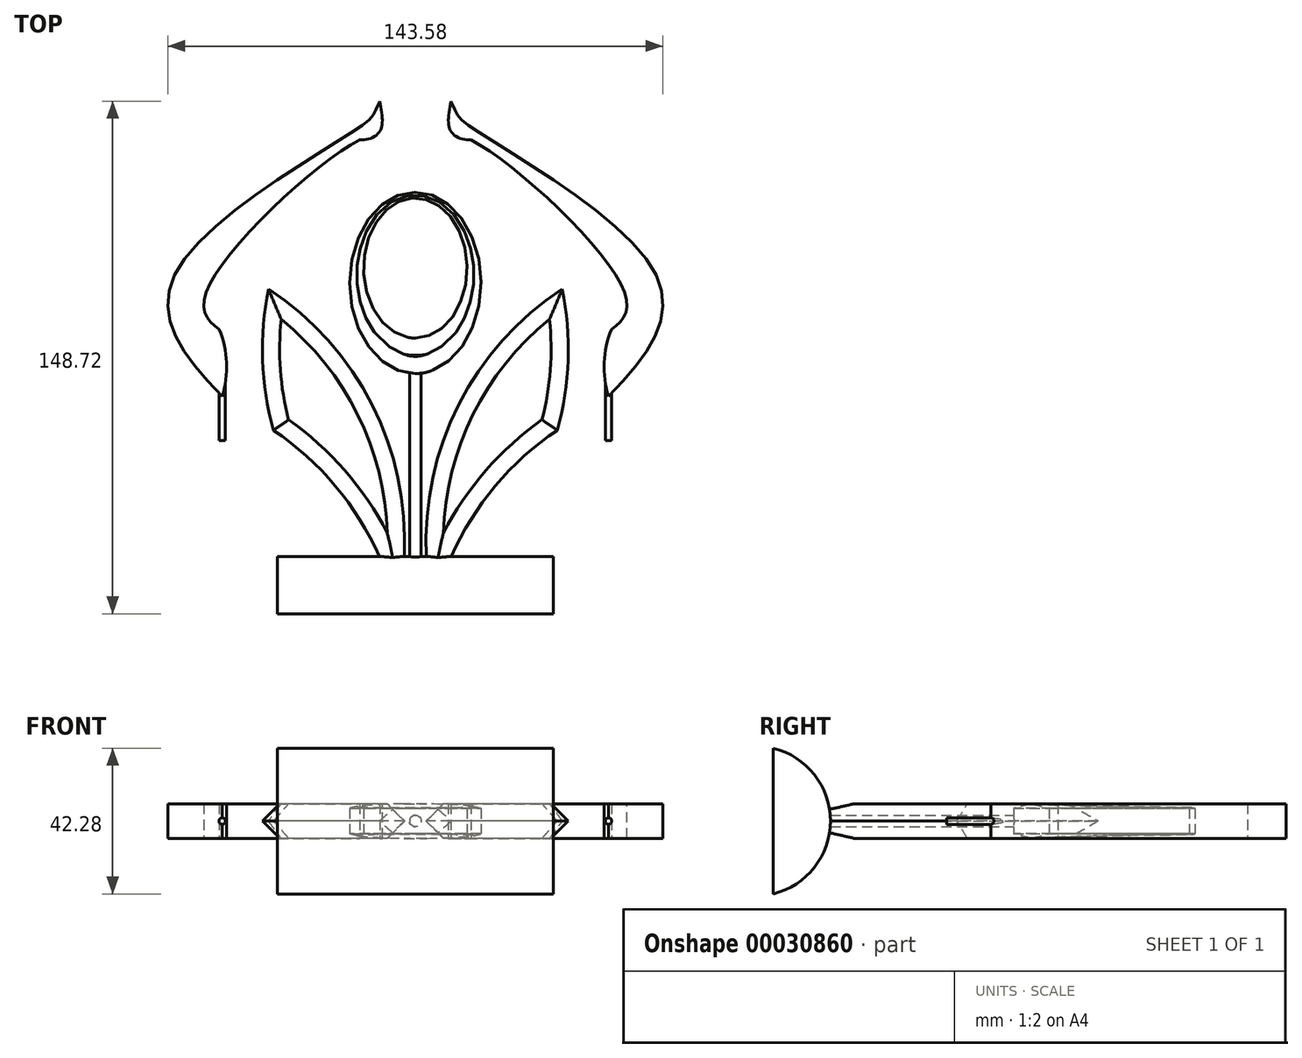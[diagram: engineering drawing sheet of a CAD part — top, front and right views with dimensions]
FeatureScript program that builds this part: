
annotation { "Feature Type Name" : "Feature", "Feature Type Description" : "" }
export const myFeature = defineFeature(function(context is Context, id is Id, definition is map)
    precondition{}
    {
        {
            var Q0;
            Q0=qCreatedBy(makeId("Top.planeOp"),FACE);
            var sketch = newSketch(context, id + "F0", { "sketchPlane" : qUnion([Q0])});
            skLineSegment(sketch, "E0", {"start": v(-75.5, -12.71) * mm, "end": v(-9.56, -74.3) * mm, "construction": true});
            skLineSegment(sketch, "E1", {"start": v(-4.86, -71.61) * mm, "end": v(-42.6, 18.94) * mm, "construction": true});
            skArc(sketch, "E2", {"start": v(-75.5, -12.71) * mm, "mid": v(-51.74, -53.37) * mm, "end": v(-9.56, -74.3) * mm});
            skArc(sketch, "E3", {"start": v(-4.86, -71.61) * mm, "mid": v(-9.83, -20.55) * mm, "end": v(-42.6, 18.94) * mm});
            skArc(sketch, "E4.MirrorCS", {"start": v(-75.5, -12.71) * mm, "mid": v(-33.32, -33.65) * mm, "end": v(-9.56, -74.3) * mm});
            skArc(sketch, "E5.0", {"start": v(-41.12, -22.06) * mm, "mid": v(-19.25, -43.28) * mm, "end": v(-6.12, -70.78) * mm});
            skArc(sketch, "E6.MirrorCS", {"start": v(-4.86, -71.61) * mm, "mid": v(-5.5, -71.2) * mm, "end": v(-6.12, -70.78) * mm});
            skArc(sketch, "E7.trimOffspring", {"start": v(-41.12, -22.06) * mm, "mid": v(-44.3, -1.65) * mm, "end": v(-42.6, 18.94) * mm});
            skArc(sketch, "E8.MirrorCS", {"start": v(75.5, -12.71) * mm, "mid": v(51.74, -53.37) * mm, "end": v(9.56, -74.3) * mm});
            skArc(sketch, "E9.MirrorCS", {"start": v(75.5, -12.71) * mm, "mid": v(33.32, -33.65) * mm, "end": v(9.56, -74.3) * mm});
            skArc(sketch, "E10.MirrorCS", {"start": v(41.12, -22.06) * mm, "mid": v(44.3, -1.65) * mm, "end": v(42.6, 18.94) * mm});
            skArc(sketch, "E11.MirrorCS", {"start": v(41.12, -22.06) * mm, "mid": v(19.25, -43.28) * mm, "end": v(6.12, -70.78) * mm});
            skArc(sketch, "E12.MirrorCS", {"start": v(4.86, -71.61) * mm, "mid": v(9.83, -20.55) * mm, "end": v(42.6, 18.94) * mm});
            skArc(sketch, "E13.MirrorCS", {"start": v(4.86, -71.61) * mm, "mid": v(5.5, -71.2) * mm, "end": v(6.12, -70.78) * mm});
            skSolve(sketch);
        }
        {
            var Q0;
            Q0=qCreatedBy(makeId("Top.planeOp"),FACE);
            var sketch = newSketch(context, id + "F1", { "sketchPlane" : qUnion([Q0])});
            skEllipse(sketch, "E14", {"center": v(0, 20.7) * mm, "majorRadius": 26.3 * mm, "minorRadius": 19.05 * mm, "majorAxis": v(0, -1)});
            skEllipse(sketch, "E15", {"center": v(0, 25) * mm, "majorRadius": 20.32 * mm, "minorRadius": 15 * mm, "majorAxis": v(0, -1)});
            skSolve(sketch);
        }
        {
            var Q0;
            Q0=qCreatedBy(makeId("Top.planeOp"),FACE);
            var sketch = newSketch(context, id + "F2", { "sketchPlane" : qUnion([Q0])});
            skFitSpline(sketch, "E16", {"points": [v(-10.32, 73.44) * mm, v(-14.62, 66.99) * mm, v(-69.19, 24.14) * mm, v(-56, -12.24) * mm], "startDerivative": vector(-33.58, -68.78) * mm, "endDerivative": vector(100.58, -102.34) * mm});
            skArc(sketch, "E17", {"start": v(-56, -12.24) * mm, "mid": v(-54.75, -2.43) * mm, "end": v(-56.87, 7.24) * mm});
            skFitSpline(sketch, "E18", {"points": [v(-56.87, 7.24) * mm, v(-60.9, 17.24) * mm, v(-16.13, 62.2) * mm], "startDerivative": vector(-32.39, 22.42) * mm, "endDerivative": vector(56.1, 28.88) * mm});
            skFitSpline(sketch, "E19", {"points": [v(-10.32, 73.44) * mm, v(-10.32, 64.63) * mm, v(-16.13, 62.2) * mm], "startDerivative": vector(3.32, -19.88) * mm, "endDerivative": vector(-13.95, 1.21) * mm});
            skFitSpline(sketch, "E20.MirrorCS", {"points": [v(10.32, 73.44) * mm, v(10.32, 64.63) * mm, v(16.13, 62.2) * mm], "startDerivative": vector(-3.32, -19.88) * mm, "endDerivative": vector(13.95, 1.21) * mm});
            skFitSpline(sketch, "E21.MirrorCS", {"points": [v(10.32, 73.44) * mm, v(14.62, 66.99) * mm, v(69.19, 24.14) * mm, v(56, -12.24) * mm], "startDerivative": vector(33.58, -68.78) * mm, "endDerivative": vector(-100.58, -102.34) * mm});
            skFitSpline(sketch, "E22.MirrorCS", {"points": [v(56.87, 7.24) * mm, v(60.9, 17.24) * mm, v(16.13, 62.2) * mm], "startDerivative": vector(32.39, 22.42) * mm, "endDerivative": vector(-56.1, 28.88) * mm});
            skArc(sketch, "E23.MirrorCS", {"start": v(56, -12.24) * mm, "mid": v(54.75, -2.43) * mm, "end": v(56.87, 7.24) * mm});
            skSolve(sketch);
        }
        {
            var Q0;
            Q0=makeQuery(id+"F2.imprint","IMPRINT",FACE,{"disambiguationData":[TD([[makeQuery(id+"F2.imprint","IMPRINT",EDGE,{"derivedFrom":sQuery(id+"F2.wireOp",EDGE,"E16")}),1.0]])]});
            var Q1;
            Q1=makeQuery(id+"F2.imprint","IMPRINT",FACE,{"disambiguationData":[TD([[makeQuery(id+"F2.imprint","IMPRINT",EDGE,{"derivedFrom":sQuery(id+"F2.wireOp",EDGE,"E20.MirrorCS")}),1.0]])]});
            var Q2;
            Q2=makeQuery(id+"F0.imprint","IMPRINT",FACE,{"disambiguationData":[TD([[makeQuery(id+"F0.imprint","IMPRINT",EDGE,{"derivedFrom":sQuery(id+"F0.wireOp",EDGE,"E3")}),1.0]])]});
            var Q3;
            Q3=makeQuery(id+"F0.imprint","IMPRINT",FACE,{"disambiguationData":[TD([[makeQuery(id+"F0.imprint","IMPRINT",EDGE,{"derivedFrom":sQuery(id+"F0.wireOp",EDGE,"E4.MirrorCS")}),-1.0]])]});
            var Q4;
            Q4=makeQuery(id+"F0.imprint","IMPRINT",FACE,{"disambiguationData":[TD([[makeQuery(id+"F0.imprint","IMPRINT",EDGE,{"derivedFrom":sQuery(id+"F0.wireOp",EDGE,"E10.MirrorCS")}),1.0]])]});
            var Q5;
            Q5=makeQuery(id+"F0.imprint","IMPRINT",FACE,{"disambiguationData":[TD([[makeQuery(id+"F0.imprint","IMPRINT",EDGE,{"derivedFrom":sQuery(id+"F0.wireOp",EDGE,"E8.MirrorCS")}),-1.0]])]});
            var Q6;
            Q6=makeQuery(id+"F1.imprint","IMPRINT",FACE,{"disambiguationData":[TD([[makeQuery(id+"F1.imprint","IMPRINT",EDGE,{"derivedFrom":sQuery(id+"F1.wireOp",EDGE,"E14")}),1.0]])]});
            extrude(context, id + "F3", {"entities" : qUnion([Q0, Q1, Q2, Q3, Q4, Q5, Q6]), "endBound" : BoundingType.SYMMETRIC, "depth" : 10 * mm});
        }
        {
            var Q0;
            Q0=makeQuery(id+"F3.opExtrude","CAP_FACE",FACE,{"disambiguationData":[OSD([sQuery(id+"F0.wireOp",EDGE,"E4.MirrorCS"),sQuery(id+"F0.wireOp",EDGE,"E2")])],"isStart":false});
            var Q1;
            Q1=makeQuery(id+"F3.opExtrude","CAP_FACE",FACE,{"disambiguationData":[OSD([sQuery(id+"F0.wireOp",EDGE,"E3"),sQuery(id+"F0.wireOp",EDGE,"E5.0"),sQuery(id+"F0.wireOp",EDGE,"E6.MirrorCS"),sQuery(id+"F0.wireOp",EDGE,"E7.trimOffspring")])],"isStart":false});
            var Q2;
            Q2=makeQuery(id+"F3.opExtrude","CAP_FACE",FACE,{"disambiguationData":[OSD([sQuery(id+"F0.wireOp",EDGE,"E10.MirrorCS"),sQuery(id+"F0.wireOp",EDGE,"E11.MirrorCS"),sQuery(id+"F0.wireOp",EDGE,"E12.MirrorCS"),sQuery(id+"F0.wireOp",EDGE,"E13.MirrorCS")])],"isStart":false});
            var Q3;
            Q3=makeQuery(id+"F3.opExtrude","CAP_FACE",FACE,{"disambiguationData":[OSD([sQuery(id+"F0.wireOp",EDGE,"E8.MirrorCS"),sQuery(id+"F0.wireOp",EDGE,"E9.MirrorCS")])],"isStart":false});
            var Q4;
            Q4=makeQuery(id+"F3.opExtrude","CAP_FACE",FACE,{"disambiguationData":[OSD([sQuery(id+"F0.wireOp",EDGE,"E8.MirrorCS"),sQuery(id+"F0.wireOp",EDGE,"E9.MirrorCS")])],"isStart":true});
            var Q5;
            Q5=makeQuery(id+"F3.opExtrude","CAP_FACE",FACE,{"disambiguationData":[OSD([sQuery(id+"F0.wireOp",EDGE,"E10.MirrorCS"),sQuery(id+"F0.wireOp",EDGE,"E11.MirrorCS"),sQuery(id+"F0.wireOp",EDGE,"E12.MirrorCS"),sQuery(id+"F0.wireOp",EDGE,"E13.MirrorCS")])],"isStart":true});
            var Q6;
            Q6=makeQuery(id+"F3.opExtrude","CAP_FACE",FACE,{"disambiguationData":[OSD([sQuery(id+"F0.wireOp",EDGE,"E3"),sQuery(id+"F0.wireOp",EDGE,"E5.0"),sQuery(id+"F0.wireOp",EDGE,"E6.MirrorCS"),sQuery(id+"F0.wireOp",EDGE,"E7.trimOffspring")])],"isStart":true});
            var Q7;
            Q7=makeQuery(id+"F3.opExtrude","CAP_FACE",FACE,{"disambiguationData":[OSD([sQuery(id+"F0.wireOp",EDGE,"E4.MirrorCS"),sQuery(id+"F0.wireOp",EDGE,"E2")])],"isStart":true});
            chamfer(context, id + "F4", {"entities" : qUnion([Q0, Q1, Q2, Q3, Q4, Q5, Q6, Q7]), "width" : 5 * mm, "tangentPropagation" : true});
        }
        {
            var Q0;
            Q0=makeQuery(id+"F3.opExtrude","CAP_FACE",FACE,{"disambiguationData":[OSD([sQuery(id+"F2.wireOp",EDGE,"E16"),sQuery(id+"F2.wireOp",EDGE,"E17"),sQuery(id+"F2.wireOp",EDGE,"E18"),sQuery(id+"F2.wireOp",EDGE,"E19")])],"isStart":false});
            var Q1;
            Q1=makeQuery(id+"F3.opExtrude","CAP_FACE",FACE,{"disambiguationData":[OSD([sQuery(id+"F2.wireOp",EDGE,"E20.MirrorCS"),sQuery(id+"F2.wireOp",EDGE,"E21.MirrorCS"),sQuery(id+"F2.wireOp",EDGE,"E22.MirrorCS"),sQuery(id+"F2.wireOp",EDGE,"E23.MirrorCS")])],"isStart":false});
            var Q2;
            Q2=makeQuery(id+"F3.opExtrude","CAP_FACE",FACE,{"disambiguationData":[OSD([sQuery(id+"F2.wireOp",EDGE,"E16"),sQuery(id+"F2.wireOp",EDGE,"E17"),sQuery(id+"F2.wireOp",EDGE,"E18"),sQuery(id+"F2.wireOp",EDGE,"E19")])],"isStart":true});
            var Q3;
            Q3=makeQuery(id+"F3.opExtrude","CAP_FACE",FACE,{"disambiguationData":[OSD([sQuery(id+"F2.wireOp",EDGE,"E20.MirrorCS"),sQuery(id+"F2.wireOp",EDGE,"E21.MirrorCS"),sQuery(id+"F2.wireOp",EDGE,"E22.MirrorCS"),sQuery(id+"F2.wireOp",EDGE,"E23.MirrorCS")])],"isStart":true});
            var Q4;
            Q4=makeQuery(id+"F3.opExtrude","CAP_FACE",FACE,{"disambiguationData":[OSD([sQuery(id+"F1.wireOp",EDGE,"E14"),sQuery(id+"F1.wireOp",EDGE,"E15")])],"isStart":true});
            var Q5;
            Q5=makeQuery(id+"F3.opExtrude","CAP_FACE",FACE,{"disambiguationData":[OSD([sQuery(id+"F1.wireOp",EDGE,"E14"),sQuery(id+"F1.wireOp",EDGE,"E15")])],"isStart":false});
            chamfer(context, id + "F5", {"entities" : qUnion([Q0, Q1, Q2, Q3, Q4, Q5]), "chamferType" : ChamferType.TWO_OFFSETS, "width1" : 1.3 * mm, "oppositeDirection" : false, "width2" : 5 * mm, "tangentPropagation" : true});
        }
        {
            var Q0;
            Q0=qCreatedBy(makeId("Right.planeOp"),FACE);
            var sketch = newSketch(context, id + "F6", { "sketchPlane" : qUnion([Q0])});
            skArc(sketch, "E24", {"start": v(-75.28, -21.14) * mm, "mid": v(-58.72, 0) * mm, "end": v(-75.28, 21.14) * mm});
            skLineSegment(sketch, "E25", {"start": v(-75.28, 21.14) * mm, "end": v(-75.28, -21.14) * mm});
            skSolve(sketch);
        }
        {
            var Q0;
            Q0 = qSketchRegion(id + "F6", true);
            extrude(context, id + "F7", {"entities" : qUnion([Q0]), "operationType" : NewBodyOperationType.ADD, "endBound" : BoundingType.SYMMETRIC, "depth" : 80 * mm});
        }
        {
            var Q0;
            Q0=qCreatedBy(makeId("Front.planeOp"),FACE);
            var sketch = newSketch(context, id + "F8", { "sketchPlane" : qUnion([Q0])});
            skCircle(sketch, "E26", {"center": v(0, 0) * mm, "radius": 1.69 * mm});
            skPoint(sketch, "E27.0", {"position": v(56, 0) * mm});
            skPoint(sketch, "E27.1", {"position": v(-56, 0) * mm});
            skCircle(sketch, "E28", {"center": v(56, 0) * mm, "radius": 0.94 * mm});
            skCircle(sketch, "E29", {"center": v(-56, 0) * mm, "radius": 0.94 * mm});
            skSolve(sketch);
        }
        {
            var Q0;
            Q0=makeQuery(id+"F8.imprint","IMPRINT",FACE,{"disambiguationData":[TD([[makeQuery(id+"F8.imprint","IMPRINT",EDGE,{"derivedFrom":sQuery(id+"F8.wireOp",EDGE,"E26")}),1.0]])]});
            var Q1;
            Q1=makeQuery(id+"F7.opExtrude","SWEPT_FACE",FACE,{"disambiguationData":[OSD([sQuery(id+"F6.wireOp",EDGE,"E25")])]});
            extrude(context, id + "F9", {"entities" : qUnion([Q0]), "operationType" : NewBodyOperationType.ADD, "endBound" : BoundingType.UP_TO_SURFACE, "endBoundEntityFace" : qUnion([Q1]), "depth" : 25 * mm});
        }
        {
            var Q0;
            Q0=makeQuery(id+"F8.imprint","IMPRINT",FACE,{"disambiguationData":[TD([[makeQuery(id+"F8.imprint","IMPRINT",EDGE,{"derivedFrom":sQuery(id+"F8.wireOp",EDGE,"E28")}),1.0]])]});
            var Q1;
            Q1=makeQuery(id+"F8.imprint","IMPRINT",FACE,{"disambiguationData":[TD([[makeQuery(id+"F8.imprint","IMPRINT",EDGE,{"derivedFrom":sQuery(id+"F8.wireOp",EDGE,"E29")}),1.0]])]});
            extrude(context, id + "F10", {"entities" : qUnion([Q0, Q1]), "operationType" : NewBodyOperationType.ADD, "depth" : 25 * mm});
        }
    });
